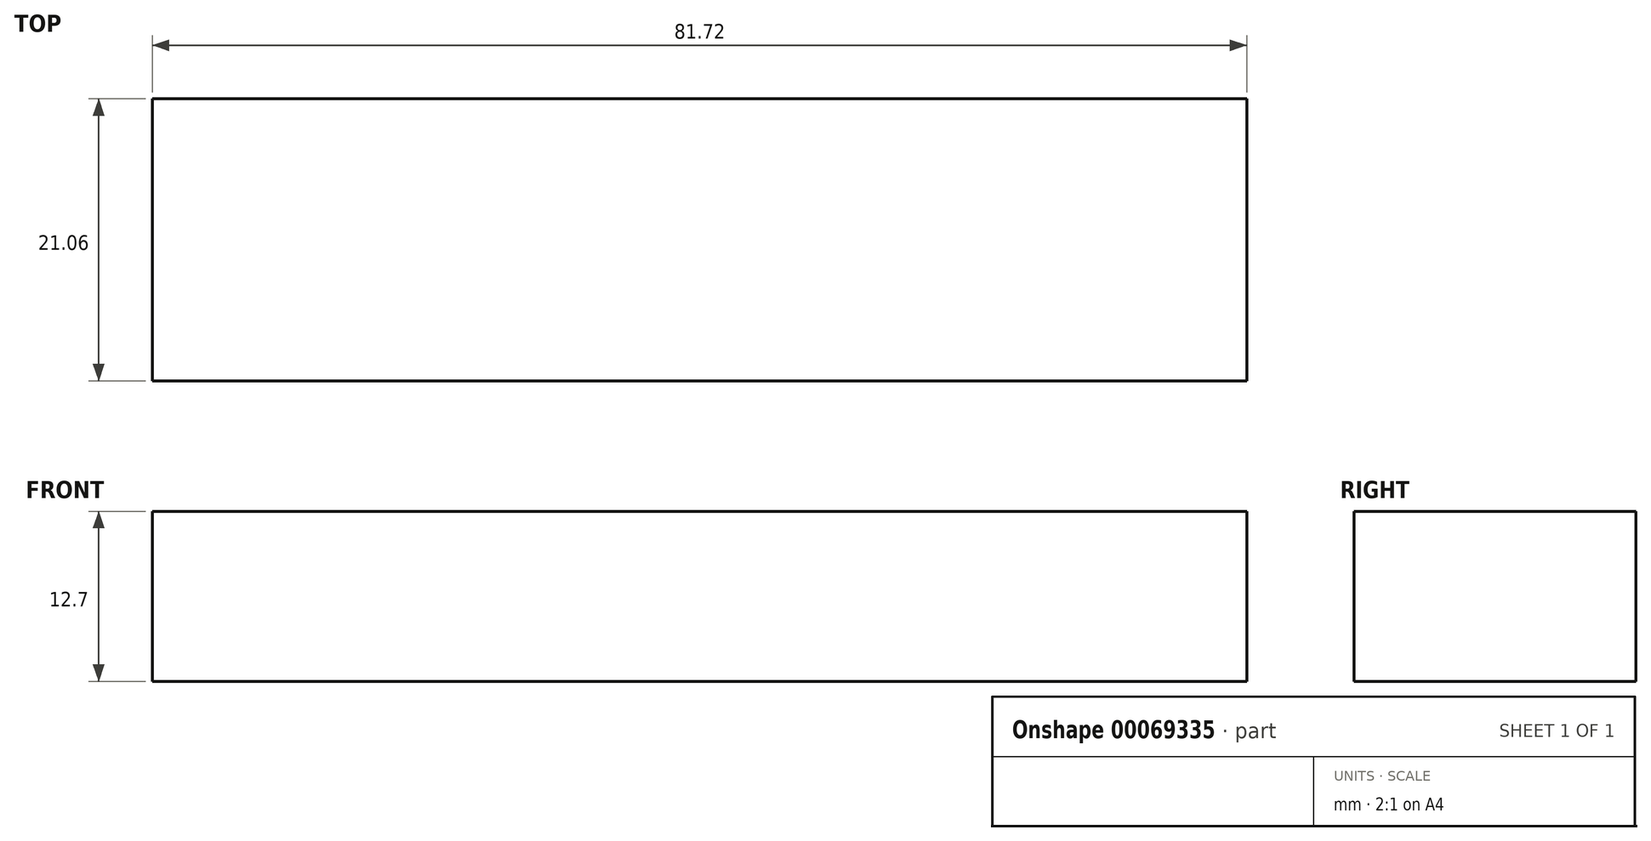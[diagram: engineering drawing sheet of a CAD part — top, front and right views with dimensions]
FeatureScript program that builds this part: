
annotation { "Feature Type Name" : "Feature", "Feature Type Description" : "" }
export const myFeature = defineFeature(function(context is Context, id is Id, definition is map)
    precondition{}
    {
        {
            var Q0;
            Q0=qCreatedBy(makeId("Top.planeOp"),FACE);
            var sketch = newSketch(context, id + "F0", { "sketchPlane" : qUnion([Q0])});
            skLineSegment(sketch, "E0.rect.bottom", {"start": v(-40.86, 10.53) * mm, "end": v(40.86, 10.53) * mm});
            skLineSegment(sketch, "E0.rect.top", {"start": v(-40.86, -10.53) * mm, "end": v(40.86, -10.53) * mm});
            skLineSegment(sketch, "E0.rect.left", {"start": v(-40.86, 10.53) * mm, "end": v(-40.86, -10.53) * mm});
            skLineSegment(sketch, "E0.rect.right", {"start": v(40.86, 10.53) * mm, "end": v(40.86, -10.53) * mm});
            skPoint(sketch, "E0.rect.middle", {"position": v(0, 0) * mm});
            skSolve(sketch);
        }
        {
            var Q0;
            Q0=makeQuery(id+"F0.imprint","IMPRINT",FACE,{"disambiguationData":[TD([[makeQuery(id+"F0.imprint","IMPRINT",EDGE,{"derivedFrom":sQuery(id+"F0.wireOp",EDGE,"E0.rect.bottom")}),-1.0]])]});
            extrude(context, id + "F1", {"entities" : qUnion([Q0]), "depth" : 12.7 * mm});
        }
    });
